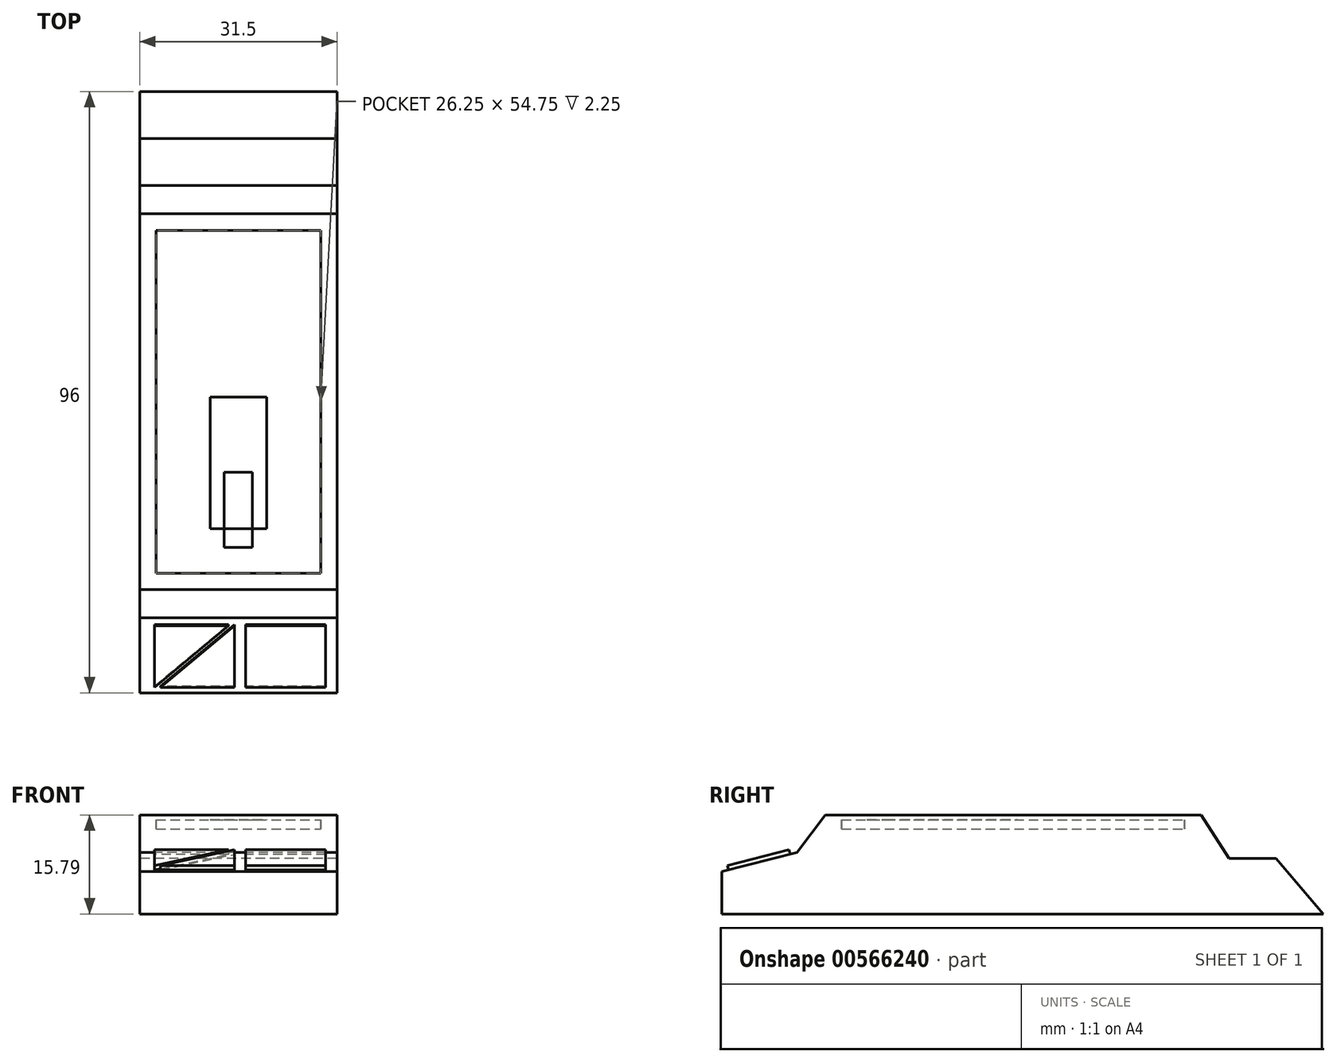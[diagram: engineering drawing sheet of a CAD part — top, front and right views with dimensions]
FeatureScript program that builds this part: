
annotation { "Feature Type Name" : "Feature", "Feature Type Description" : "" }
export const myFeature = defineFeature(function(context is Context, id is Id, definition is map)
    precondition{}
    {
        {
            var Q0;
            Q0=qCreatedBy(makeId("Right.planeOp"),FACE);
            var sketch = newSketch(context, id + "F0", { "sketchPlane" : qUnion([Q0])});
            skLineSegment(sketch, "E0", {"start": v(71.86, -7.61) * mm, "end": v(61.86, 4.22) * mm});
            skLineSegment(sketch, "E1", {"start": v(61.86, 4.22) * mm, "end": v(51.86, 4.22) * mm});
            skLineSegment(sketch, "E2", {"start": v(51.86, 4.22) * mm, "end": v(45.86, 13.44) * mm});
            skLineSegment(sketch, "E3", {"start": v(45.86, 13.44) * mm, "end": v(-34.14, 13.44) * mm});
            skLineSegment(sketch, "E4", {"start": v(-34.14, 13.44) * mm, "end": v(-40.14, 5.44) * mm});
            skLineSegment(sketch, "E5", {"start": v(-40.14, 5.44) * mm, "end": v(-56.14, 1.38) * mm});
            skLineSegment(sketch, "E6", {"start": v(-56.14, 1.38) * mm, "end": v(-56.14, -7.61) * mm});
            skLineSegment(sketch, "E7", {"start": v(-56.14, 1.38) * mm, "end": v(-40.14, 1.38) * mm, "construction": true});
            skLineSegment(sketch, "E8", {"start": v(-40.14, 1.38) * mm, "end": v(-40.14, 5.44) * mm, "construction": true});
            skLineSegment(sketch, "E9", {"start": v(-40.14, 5.44) * mm, "end": v(-34.14, 5.44) * mm, "construction": true});
            skLineSegment(sketch, "E10", {"start": v(-34.14, 5.44) * mm, "end": v(-34.14, 13.44) * mm, "construction": true});
            skLineSegment(sketch, "E11", {"start": v(45.86, 13.44) * mm, "end": v(45.86, 4.22) * mm, "construction": true});
            skLineSegment(sketch, "E12", {"start": v(45.86, 4.22) * mm, "end": v(51.86, 4.22) * mm, "construction": true});
            skLineSegment(sketch, "E13", {"start": v(61.86, 4.22) * mm, "end": v(61.86, -7.61) * mm, "construction": true});
            skLineSegment(sketch, "E14", {"start": v(61.86, -7.61) * mm, "end": v(71.86, -7.61) * mm});
            skLineSegment(sketch, "E15", {"start": v(-56.14, -7.61) * mm, "end": v(61.86, -7.61) * mm});
            skSolve(sketch);
        }
        {
            var Q0;
            Q0=qCreatedBy(makeId("Right.planeOp"),FACE);
            var sketch = newSketch(context, id + "F1", { "sketchPlane" : qUnion([Q0])});
            skLineSegment(sketch, "E16.0", {"start": v(45.86, 13.44) * mm, "end": v(-34.14, 13.44) * mm});
            skLineSegment(sketch, "E16.1", {"start": v(-34.14, 13.44) * mm, "end": v(-40.14, 5.44) * mm});
            skLineSegment(sketch, "E16.2", {"start": v(-40.14, 5.44) * mm, "end": v(-56.14, 1.38) * mm});
            skLineSegment(sketch, "E16.3", {"start": v(-56.14, 1.38) * mm, "end": v(-56.14, -7.61) * mm});
            skLineSegment(sketch, "E16.4", {"start": v(-56.14, -7.61) * mm, "end": v(61.86, -7.61) * mm});
            skLineSegment(sketch, "E16.5", {"start": v(51.86, 4.22) * mm, "end": v(45.86, 13.44) * mm});
            skLineSegment(sketch, "E16.6", {"start": v(61.86, 4.22) * mm, "end": v(51.86, 4.22) * mm});
            skLineSegment(sketch, "E16.7", {"start": v(71.86, -7.61) * mm, "end": v(61.86, 4.22) * mm});
            skLineSegment(sketch, "E16.8", {"start": v(61.86, -7.61) * mm, "end": v(71.86, -7.61) * mm});
            skText(sketch, "E17", { "text": "front", "fontName": "OpenSans-Regular.ttf"});
            const initialGuessF1  = {"E17": [-0.05367, 0.01505, 1, 0, 0.0049]};
            skSetInitialGuess(sketch, initialGuessF1);
            skSolve(sketch);
        }
        {
            var Q0;
            Q0=makeQuery(id+"F1.imprint","IMPRINT",FACE,{"disambiguationData":[TD([[makeQuery(id+"F1.imprint","IMPRINT",EDGE,{"derivedFrom":sQuery(id+"F1.wireOp",EDGE,"E16.0")}),1.0]])]});
            extrude(context, id + "F2", {"entities" : qUnion([Q0]), "depth" : 42 * mm, "offsetDistance" : 25 * mm});
        }
        {
            var Q0;
            Q0=makeQuery(id+"F2.opExtrude","SWEPT_FACE",FACE,{"disambiguationData":[OSD([sQuery(id+"F1.wireOp",EDGE,"E16.0")])]});
            var sketch = newSketch(context, id + "F3", { "sketchPlane" : qUnion([Q0])});
            skLineSegment(sketch, "E18.bottom", {"start": v(3.5, -30.64) * mm, "end": v(38.5, -30.64) * mm});
            skLineSegment(sketch, "E18.top", {"start": v(3.5, 42.36) * mm, "end": v(38.5, 42.36) * mm});
            skLineSegment(sketch, "E18.left", {"start": v(3.5, -30.64) * mm, "end": v(3.5, 42.36) * mm});
            skLineSegment(sketch, "E18.right", {"start": v(38.5, -30.64) * mm, "end": v(38.5, 42.36) * mm});
            skLineSegment(sketch, "E19.0", {"start": v(0, 45.86) * mm, "end": v(0, -34.14) * mm});
            skLineSegment(sketch, "E19.1", {"start": v(42, -34.14) * mm, "end": v(0, -34.14) * mm});
            skLineSegment(sketch, "E19.2", {"start": v(42, 45.86) * mm, "end": v(42, -34.14) * mm});
            skLineSegment(sketch, "E19.3", {"start": v(42, 45.86) * mm, "end": v(0, 45.86) * mm});
            skLineSegment(sketch, "E20", {"start": v(3.5, 5.86) * mm, "end": v(0, 5.86) * mm, "construction": true});
            skLineSegment(sketch, "E21", {"start": v(21, -30.64) * mm, "end": v(21, -34.14) * mm, "construction": true});
            skLineSegment(sketch, "E22", {"start": v(38.5, 5.86) * mm, "end": v(42, 5.86) * mm, "construction": true});
            skLineSegment(sketch, "E23", {"start": v(21, 42.36) * mm, "end": v(21, 45.86) * mm, "construction": true});
            skPoint(sketch, "E23.endSnap0", {"position": v(21, 45.86) * mm});
            skSolve(sketch);
        }
        {
            var Q0;
            Q0=makeQuery(id+"F3.imprint","IMPRINT",FACE,{"disambiguationData":[TD([[makeQuery(id+"F3.imprint","IMPRINT",EDGE,{"derivedFrom":sQuery(id+"F3.wireOp",EDGE,"E18.bottom")}),1.0]])]});
            extrude(context, id + "F4", {"entities" : qUnion([Q0]), "operationType" : NewBodyOperationType.REMOVE, "oppositeDirection" : true, "depth" : 3 * mm, "offsetDistance" : 25 * mm});
        }
        {
            var Q0;
            Q0=makeQuery(id+"F2.opExtrude","SWEPT_FACE",FACE,{"disambiguationData":[OSD([sQuery(id+"F1.wireOp",EDGE,"E16.2")])]});
            var sketch = newSketch(context, id + "F5", { "sketchPlane" : qUnion([Q0])});
            skLineSegment(sketch, "E24.bottom", {"start": v(39.58, -52.57) * mm, "end": v(22.58, -52.57) * mm});
            skLineSegment(sketch, "E24.top", {"start": v(39.58, -39.07) * mm, "end": v(22.58, -39.07) * mm});
            skLineSegment(sketch, "E24.left", {"start": v(39.58, -52.57) * mm, "end": v(39.58, -39.07) * mm});
            skLineSegment(sketch, "E24.right", {"start": v(22.58, -52.57) * mm, "end": v(22.58, -39.07) * mm});
            skLineSegment(sketch, "E25.bottom", {"start": v(20.15, -52.57) * mm, "end": v(4.4, -52.57) * mm});
            skLineSegment(sketch, "E25.top", {"start": v(18.9, -39.07) * mm, "end": v(3.15, -39.07) * mm});
            skLineSegment(sketch, "E25.left", {"start": v(20.15, -52.57) * mm, "end": v(20.15, -39.07) * mm});
            skLineSegment(sketch, "E26", {"start": v(2.42, -45.82) * mm, "end": v(0, -45.82) * mm, "construction": true});
            skLineSegment(sketch, "E27", {"start": v(20.15, -45.82) * mm, "end": v(22.58, -45.82) * mm, "construction": true});
            skLineSegment(sketch, "E28", {"start": v(39.58, -45.82) * mm, "end": v(42, -45.82) * mm, "construction": true});
            skLineSegment(sketch, "E29", {"start": v(11.03, -39.07) * mm, "end": v(11.03, -37.57) * mm, "construction": true});
            skLineSegment(sketch, "E30", {"start": v(12.28, -52.57) * mm, "end": v(12.28, -54.07) * mm, "construction": true});
            skLineSegment(sketch, "E31", {"start": v(4.4, -52.57) * mm, "end": v(20.15, -39.07) * mm});
            skLineSegment(sketch, "E32", {"start": v(3.15, -52.57) * mm, "end": v(18.9, -39.07) * mm});
            skLineSegment(sketch, "E33", {"start": v(3.15, -52.57) * mm, "end": v(3.15, -39.07) * mm});
            skLineSegment(sketch, "E34", {"start": v(4.4, -52.57) * mm, "end": v(3.15, -52.57) * mm, "construction": true});
            skLineSegment(sketch, "E35", {"start": v(20.15, -39.07) * mm, "end": v(18.9, -39.07) * mm, "construction": true});
            skLineSegment(sketch, "E36", {"start": v(31.08, -52.57) * mm, "end": v(31.08, -54.07) * mm, "construction": true});
            skLineSegment(sketch, "E37", {"start": v(31.08, -39.07) * mm, "end": v(31.08, -37.57) * mm, "construction": true});
            skLineSegment(sketch, "E38", {"start": v(3.15, -45.82) * mm, "end": v(20.15, -45.82) * mm, "construction": true});
            skLineSegment(sketch, "E39", {"start": v(2.42, -45.82) * mm, "end": v(3.15, -45.82) * mm, "construction": true});
            skSolve(sketch);
        }
        {
            var Q0;
            Q0=makeQuery(id+"F5.imprint","IMPRINT",FACE,{"disambiguationData":[TD([[makeQuery(id+"F5.imprint","IMPRINT",EDGE,{"derivedFrom":sQuery(id+"F5.wireOp",EDGE,"E25.top")}),1.0]])]});
            var Q1;
            Q1=makeQuery(id+"F5.imprint","IMPRINT",FACE,{"disambiguationData":[TD([[makeQuery(id+"F5.imprint","IMPRINT",EDGE,{"derivedFrom":sQuery(id+"F5.wireOp",EDGE,"E25.bottom")}),-1.0]])]});
            var Q2;
            Q2=makeQuery(id+"F5.imprint","IMPRINT",FACE,{"disambiguationData":[TD([[makeQuery(id+"F5.imprint","IMPRINT",EDGE,{"derivedFrom":sQuery(id+"F5.wireOp",EDGE,"E24.bottom")}),-1.0]])]});
            extrude(context, id + "F6", {"entities" : qUnion([Q0, Q1, Q2]), "depth" : 1 * mm, "offsetDistance" : 25 * mm});
        }
        {
            var Q0;
            Q0=makeQuery(id+"F4.boolean.opBoolean","COPY",FACE,{"derivedFrom":makeQuery(id+"F4.opExtrude","CAP_FACE",FACE,{"disambiguationData":[OSD([sQuery(id+"F3.wireOp",EDGE,"E18.bottom"),sQuery(id+"F3.wireOp",EDGE,"E18.top"),sQuery(id+"F3.wireOp",EDGE,"E18.left"),sQuery(id+"F3.wireOp",EDGE,"E18.right")])],"isStart":false})});
            var sketch = newSketch(context, id + "F7", { "sketchPlane" : qUnion([Q0])});
            skLineSegment(sketch, "E40.0", {"start": v(3.5, -30.64) * mm, "end": v(3.5, 42.36) * mm});
            skLineSegment(sketch, "E40.1", {"start": v(3.5, -30.64) * mm, "end": v(38.5, -30.64) * mm});
            skLineSegment(sketch, "E40.2", {"start": v(38.5, -30.64) * mm, "end": v(38.5, 42.36) * mm});
            skLineSegment(sketch, "E40.3", {"start": v(3.5, 42.36) * mm, "end": v(38.5, 42.36) * mm});
            skSolve(sketch);
        }
        {
            var Q0;
            Q0=makeQuery(id+"F7.imprint","IMPRINT",FACE,{"disambiguationData":[TD([[makeQuery(id+"F7.imprint","IMPRINT",EDGE,{"derivedFrom":sQuery(id+"F7.wireOp",EDGE,"E40.0")}),-1.0]])]});
            extrude(context, id + "F8", {"entities" : qUnion([Q0]), "depth" : 2 * mm, "offsetDistance" : 25 * mm});
        }
        {
            var Q0;
            Q0=makeQuery(id+"F8.opExtrude","CAP_FACE",FACE,{"disambiguationData":[OSD([sQuery(id+"F7.wireOp",EDGE,"E40.0"),sQuery(id+"F7.wireOp",EDGE,"E40.1"),sQuery(id+"F7.wireOp",EDGE,"E40.2"),sQuery(id+"F7.wireOp",EDGE,"E40.3")])],"isStart":false});
            var sketch = newSketch(context, id + "F9", { "sketchPlane" : qUnion([Q0])});
            skLineSegment(sketch, "E41.bottom", {"start": v(18, -25.18) * mm, "end": v(24, -25.18) * mm});
            skLineSegment(sketch, "E41.left", {"start": v(18, -25.18) * mm, "end": v(18, -21.18) * mm});
            skLineSegment(sketch, "E41.right", {"start": v(24, -25.18) * mm, "end": v(24, -21.18) * mm});
            skLineSegment(sketch, "E42.top", {"start": v(15, 6.82) * mm, "end": v(27, 6.82) * mm});
            skLineSegment(sketch, "E42.left", {"start": v(15, -21.18) * mm, "end": v(15, 6.82) * mm});
            skLineSegment(sketch, "E42.right", {"start": v(27, -21.18) * mm, "end": v(27, 6.82) * mm});
            skLineSegment(sketch, "E43", {"start": v(15, -21.18) * mm, "end": v(18, -21.18) * mm});
            skLineSegment(sketch, "E44", {"start": v(24, -21.18) * mm, "end": v(18, -21.18) * mm});
            skLineSegment(sketch, "E45", {"start": v(24, -21.18) * mm, "end": v(27, -21.18) * mm});
            skLineSegment(sketch, "E46", {"start": v(24, -21.18) * mm, "end": v(24, -9.18) * mm});
            skLineSegment(sketch, "E47", {"start": v(18, -21.18) * mm, "end": v(18, -9.18) * mm});
            skLineSegment(sketch, "E48", {"start": v(18, -9.18) * mm, "end": v(24, -9.18) * mm});
            skLineSegment(sketch, "E49", {"start": v(15, -7.18) * mm, "end": v(3.5, -7.18) * mm, "construction": true});
            skLineSegment(sketch, "E50", {"start": v(27, -7.18) * mm, "end": v(38.5, -7.18) * mm, "construction": true});
            skSolve(sketch);
        }
        {
            var Q0;
            Q0=makeQuery(id+"F9.imprint","IMPRINT",FACE,{"disambiguationData":[TD([[makeQuery(id+"F9.imprint","IMPRINT",EDGE,{"derivedFrom":sQuery(id+"F9.wireOp",EDGE,"E42.top")}),-1.0]])]});
            var Q1;
            Q1=makeQuery(id+"F9.imprint","IMPRINT",FACE,{"disambiguationData":[TD([[makeQuery(id+"F9.imprint","IMPRINT",EDGE,{"derivedFrom":sQuery(id+"F9.wireOp",EDGE,"E41.bottom")}),1.0]])]});
            extrude(context, id + "F10", {"entities" : qUnion([Q0, Q1]), "depth" : .1 * mm, "offsetDistance" : 25 * mm});
        }
        {
            var Q0;
            Q0=makeQuery(id+"F6.opExtrude","SWEPT_BODY",BODY,{"disambiguationData":[OSD([sQuery(id+"F5.wireOp",EDGE,"E25.top"),sQuery(id+"F5.wireOp",EDGE,"E32"),sQuery(id+"F5.wireOp",EDGE,"E33")])]});
            var Q1;
            Q1=makeQuery(id+"F6.opExtrude","SWEPT_BODY",BODY,{"disambiguationData":[OSD([sQuery(id+"F5.wireOp",EDGE,"E25.bottom"),sQuery(id+"F5.wireOp",EDGE,"E25.left"),sQuery(id+"F5.wireOp",EDGE,"E31")])]});
            var Q2;
            Q2=makeQuery(id+"F6.opExtrude","SWEPT_BODY",BODY,{"disambiguationData":[OSD([sQuery(id+"F5.wireOp",EDGE,"E24.bottom"),sQuery(id+"F5.wireOp",EDGE,"E24.top"),sQuery(id+"F5.wireOp",EDGE,"E24.left"),sQuery(id+"F5.wireOp",EDGE,"E24.right")])]});
            var Q3;
            Q3=makeQuery(id+"F8.opExtrude","SWEPT_BODY",BODY,{"disambiguationData":[OSD([sQuery(id+"F7.wireOp",EDGE,"E40.0"),sQuery(id+"F7.wireOp",EDGE,"E40.1"),sQuery(id+"F7.wireOp",EDGE,"E40.2"),sQuery(id+"F7.wireOp",EDGE,"E40.3")])]});
            var Q4;
            Q4=makeQuery(id+"F10.opExtrude","SWEPT_BODY",BODY,{"disambiguationData":[OSD([sQuery(id+"F9.wireOp",EDGE,"E41.bottom"),sQuery(id+"F9.wireOp",EDGE,"E41.left"),sQuery(id+"F9.wireOp",EDGE,"E41.right"),sQuery(id+"F9.wireOp",EDGE,"E44")])]});
            var Q5;
            Q5=makeQuery(id+"F10.opExtrude","SWEPT_BODY",BODY,{"disambiguationData":[OSD([sQuery(id+"F9.wireOp",EDGE,"E42.top"),sQuery(id+"F9.wireOp",EDGE,"E42.left"),sQuery(id+"F9.wireOp",EDGE,"E42.right"),sQuery(id+"F9.wireOp",EDGE,"E43"),sQuery(id+"F9.wireOp",EDGE,"E45"),sQuery(id+"F9.wireOp",EDGE,"E46"),sQuery(id+"F9.wireOp",EDGE,"E47"),sQuery(id+"F9.wireOp",EDGE,"E48")])]});
            var Q6;
            Q6=makeQuery(id+"F2.opExtrude","SWEPT_BODY",BODY,{"disambiguationData":[OSD([sQuery(id+"F1.wireOp",EDGE,"E16.0"),sQuery(id+"F1.wireOp",EDGE,"E16.1"),sQuery(id+"F1.wireOp",EDGE,"E16.2"),sQuery(id+"F1.wireOp",EDGE,"E16.3"),sQuery(id+"F1.wireOp",EDGE,"E16.4"),sQuery(id+"F1.wireOp",EDGE,"E16.5"),sQuery(id+"F1.wireOp",EDGE,"E16.6"),sQuery(id+"F1.wireOp",EDGE,"E16.7"),sQuery(id+"F1.wireOp",EDGE,"E16.8")])]});
            var Q7;
            Q7=makeQuery(id+"F2.opExtrude","CAP_VERTEX",VERTEX,{"disambiguationData":[OSD([sQuery(id+"F1.wireOp",EDGE,"E16.7"),sQuery(id+"F1.wireOp",EDGE,"E16.8")])],"isStart":false});
            transform(context, id + "F11", {"entities" : qUnion([Q0, Q1, Q2, Q3, Q4, Q5, Q6]), "transformType" : TransformType.SCALE_UNIFORMLY, "scale" : 90 / 120, "scalePoint" : qUnion([Q7]), "makeCopy" : false});
        }
    });
